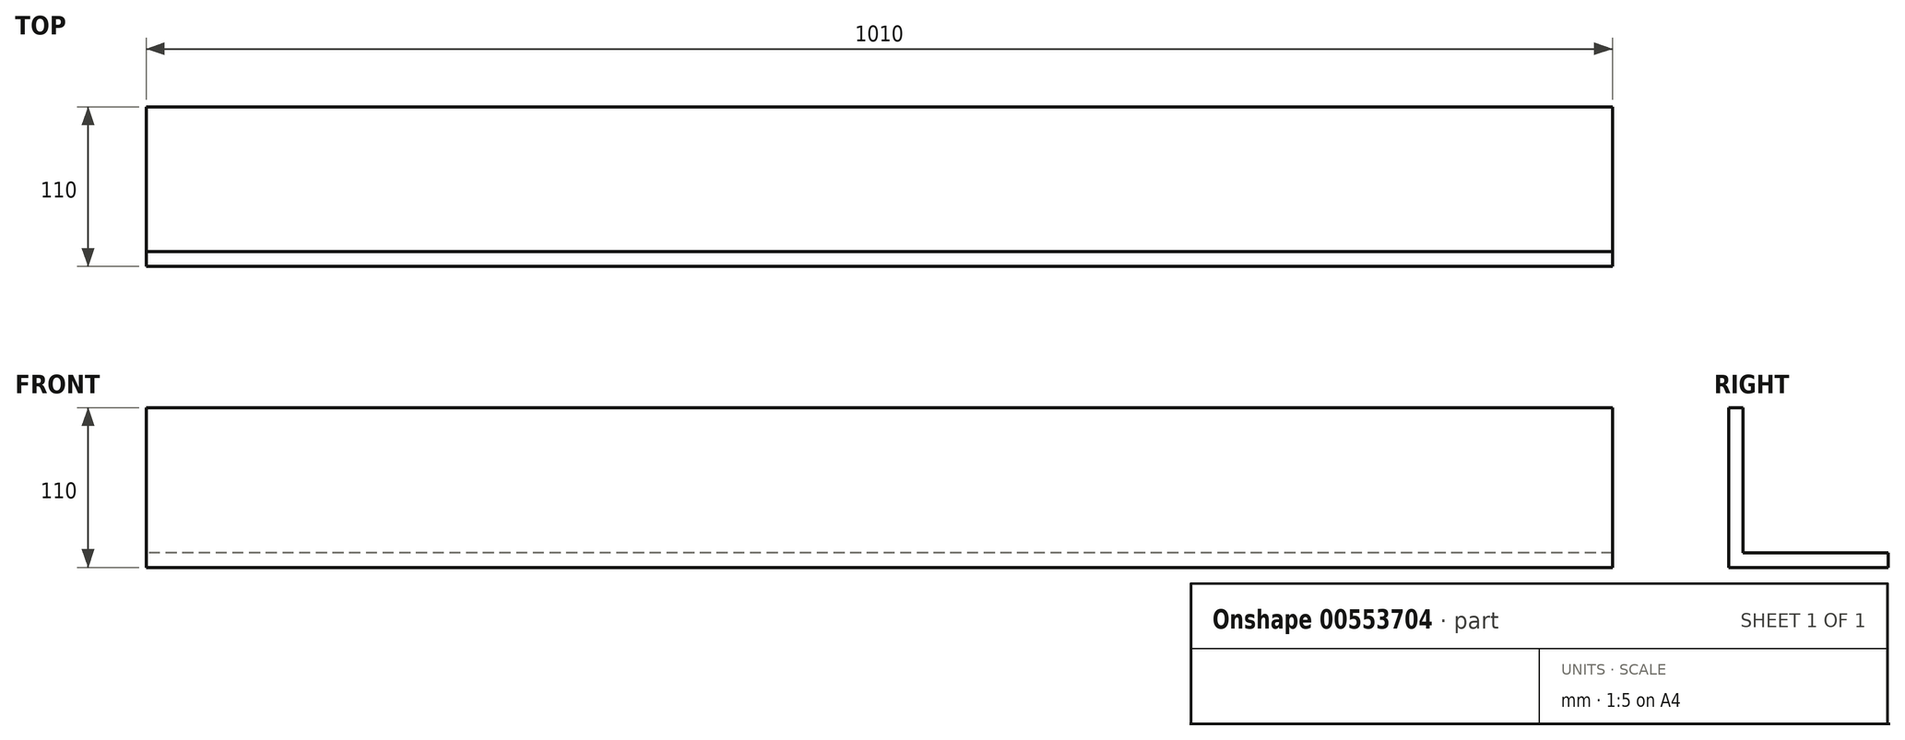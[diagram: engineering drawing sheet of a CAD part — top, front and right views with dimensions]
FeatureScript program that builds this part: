
annotation { "Feature Type Name" : "Feature", "Feature Type Description" : "" }
export const myFeature = defineFeature(function(context is Context, id is Id, definition is map)
    precondition{}
    {
        {
            var Q0;
            Q0=qCreatedBy(makeId("Right.planeOp"),FACE);
            var sketch = newSketch(context, id + "F0", { "sketchPlane" : qUnion([Q0])});
            skLineSegment(sketch, "E0.bottom", {"start": v(0, 0) * mm, "end": v(10, 0) * mm});
            skLineSegment(sketch, "E0.top", {"start": v(0, 110) * mm, "end": v(10, 110) * mm});
            skLineSegment(sketch, "E0.left", {"start": v(0, 0) * mm, "end": v(0, 110) * mm});
            skLineSegment(sketch, "E0.right", {"start": v(10, 10) * mm, "end": v(10, 110) * mm});
            skLineSegment(sketch, "E1.bottom", {"start": v(0, 0) * mm, "end": v(110, 0) * mm});
            skLineSegment(sketch, "E1.top", {"start": v(10, 10) * mm, "end": v(110, 10) * mm});
            skLineSegment(sketch, "E1.left", {"start": v(0, 0) * mm, "end": v(0, 10) * mm});
            skLineSegment(sketch, "E1.right", {"start": v(110, 0) * mm, "end": v(110, 10) * mm});
            skSolve(sketch);
        }
        {
            var Q0;
            Q0=makeQuery(id+"F0.imprint","IMPRINT",FACE,{"disambiguationData":[TD([[makeQuery(id+"F0.imprint","IMPRINT",EDGE,{"derivedFrom":sQuery(id+"F0.wireOp",EDGE,"E0.top")}),-1.0]])]});
            extrude(context, id + "F1", {"entities" : qUnion([Q0]), "depth" : 1010 * mm, "offsetDistance" : 25 * mm});
        }
    });
